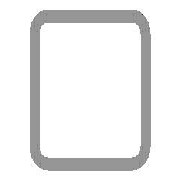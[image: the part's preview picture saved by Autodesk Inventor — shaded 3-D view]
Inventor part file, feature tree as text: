
AUTODESK INVENTOR PART (.ipt)
format: ipt  version: 2022 (Build 260153000, 153)  size: 176,640 bytes
history: native  units: mm (DEFAULTED — no unit token found)
features: other x5, sketch x2, sweep x1, plane x1
ambient origin geometry x8: Origin, YZ Plane, XZ Plane, XY Plane, X Axis, Y Axis, Z Axis, Center Point
bodies: Solid1 (feature_tree), Body (feature_tree)
feature tree (9):
  parser-record x1  (decoder bookkeeping rows leaked as tree rows — omitted from the tree; the rows remain in map.json)
  other  "Driven Length"
  other  "Start Plane"
  other  "End Plane"
  sweep  "Sweep Path"
  other  "Orientation Work Plane"
  sketch  "Sketch3"  dims[d7=8.0mm d9=40.0mm]
  plane  "Work Plane3"
  sketch  "Sketch4"  dims[d11=40.0mm d12=4.0mm d13=-0.0mm d14=3515.406592mm d15=20.0mm d16=20.0mm d17=90.0deg d18=3515.406592mm d19=0.0mm d20=0.0mm]
